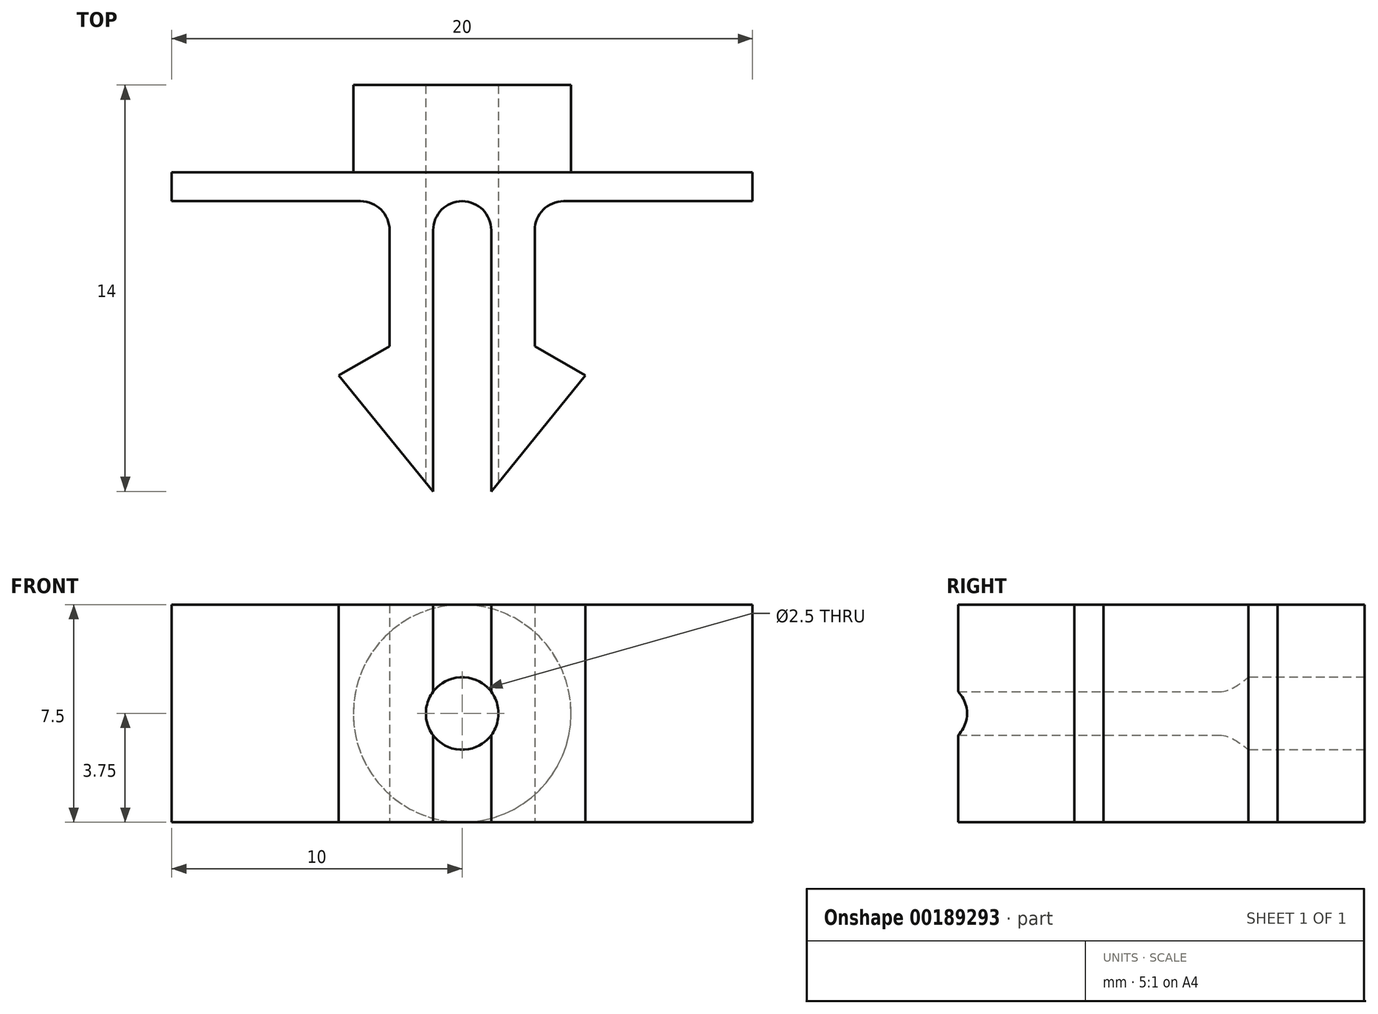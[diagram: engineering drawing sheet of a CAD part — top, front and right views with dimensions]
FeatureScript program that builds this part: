
annotation { "Feature Type Name" : "Feature", "Feature Type Description" : "" }
export const myFeature = defineFeature(function(context is Context, id is Id, definition is map)
    precondition{}
    {
        {
            var Q0;
            Q0=qCreatedBy(makeId("Top.planeOp"),FACE);
            var sketch = newSketch(context, id + "F0", { "sketchPlane" : qUnion([Q0])});
            skLineSegment(sketch, "E0", {"start": v(-1, 0) * mm, "end": v(-1, 9) * mm});
            skLineSegment(sketch, "E1", {"start": v(1, 9) * mm, "end": v(1, 0) * mm});
            skPoint(sketch, "E2", {"position": v(-1, 5) * mm});
            skPoint(sketch, "E3", {"position": v(1, 5) * mm});
            skLineSegment(sketch, "E4", {"start": v(-2.5, 5) * mm, "end": v(-2.5, 10) * mm});
            skLineSegment(sketch, "E5", {"start": v(2.5, 10) * mm, "end": v(2.5, 5) * mm});
            skLineSegment(sketch, "E6", {"start": v(-4.25, 4) * mm, "end": v(4.25, 4) * mm, "construction": true});
            skPoint(sketch, "E7", {"position": v(0, 4) * mm});
            skArc(sketch, "E8", {"start": v(1, 9) * mm, "mid": v(0, 10) * mm, "end": v(-1, 9) * mm});
            skLineSegment(sketch, "E9", {"start": v(1, 0) * mm, "end": v(4.25, 4) * mm});
            skLineSegment(sketch, "E10", {"start": v(2.5, 5) * mm, "end": v(4.25, 4) * mm});
            skLineSegment(sketch, "E11", {"start": v(-2.5, 5) * mm, "end": v(-4.25, 4) * mm});
            skLineSegment(sketch, "E12", {"start": v(-4.25, 4) * mm, "end": v(-1, 0) * mm});
            skLineSegment(sketch, "E13", {"start": v(-2.5, 10) * mm, "end": v(-10, 10) * mm});
            skLineSegment(sketch, "E14", {"start": v(-10, 10) * mm, "end": v(-10, 11) * mm});
            skLineSegment(sketch, "E15", {"start": v(-10, 11) * mm, "end": v(10, 11) * mm});
            skLineSegment(sketch, "E16", {"start": v(10, 11) * mm, "end": v(10, 10) * mm});
            skLineSegment(sketch, "E17", {"start": v(10, 10) * mm, "end": v(2.5, 10) * mm});
            skPoint(sketch, "E18", {"position": v(0, 11) * mm});
            skPoint(sketch, "E19", {"position": v(0, 10) * mm});
            skSolve(sketch);
        }
        {
            var Q0;
            Q0=makeQuery(id+"F0.imprint","IMPRINT",FACE,{"disambiguationData":[TD([[makeQuery(id+"F0.imprint","IMPRINT",EDGE,{"derivedFrom":sQuery(id+"F0.wireOp",EDGE,"E0")}),1.0]])]});
            extrude(context, id + "F1", {"entities" : qUnion([Q0]), "depth" : 7.5 * mm});
        }
        {
            var Q0;
            Q0=makeQuery(id+"F1.opExtrude","SWEPT_EDGE",EDGE,{"disambiguationData":[OSD([sQuery(id+"F0.wireOp",EDGE,"E5"),sQuery(id+"F0.wireOp",EDGE,"E17")])]});
            var Q1;
            Q1=makeQuery(id+"F1.opExtrude","SWEPT_EDGE",EDGE,{"disambiguationData":[OSD([sQuery(id+"F0.wireOp",EDGE,"E4"),sQuery(id+"F0.wireOp",EDGE,"E13")])]});
            fillet(context, id + "F2", {"entities" : qUnion([Q0, Q1]), "radius" : 1 * mm, "tangentPropagation" : true, "allowEdgeOverflow" : false});
        }
        {
            var Q0;
            Q0=makeQuery(id+"F1.opExtrude","SWEPT_FACE",FACE,{"disambiguationData":[OSD([sQuery(id+"F0.wireOp",EDGE,"E15")])]});
            var sketch = newSketch(context, id + "F3", { "sketchPlane" : qUnion([Q0])});
            skLineSegment(sketch, "E20", {"start": v(0, 7.5) * mm, "end": v(0, 0) * mm, "construction": true});
            skPoint(sketch, "E21", {"position": v(0, 3.75) * mm});
            skCircle(sketch, "E22", {"center": v(0, 3.75) * mm, "radius": 3.75 * mm});
            skCircle(sketch, "E23", {"center": v(0, 3.75) * mm, "radius": 1.25 * mm});
            skSolve(sketch);
        }
        {
            var Q0;
            {var subQ0=sQuery(id+"F3.wireOp",EDGE,"E22");var subQ1=sQuery(id+"F0.wireOp",EDGE,"E15");var subQ2=makeQuery(id+"F3.imprint","INTERSECT",VERTEX,{"derivedFrom":[makeQuery(id+"F1.opExtrude","CAP_EDGE",EDGE,{"disambiguationData":[OSD([subQ1])],"isStart":true}),subQ0]});Q0=makeQuery(id+"F3.imprint","IMPRINT",FACE,{"disambiguationData":[TD([[makeQuery(id+"F3.imprint","IMPRINT",EDGE,{"disambiguationData":[TD([[subQ2,1.0]])],"derivedFrom":subQ0}),1.0]])]});}
            extrude(context, id + "F4", {"entities" : qUnion([Q0]), "operationType" : NewBodyOperationType.ADD, "depth" : 3 * mm});
        }
        {
            var Q0;
            Q0=makeQuery(id+"F3.imprint","IMPRINT",FACE,{"disambiguationData":[TD([[makeQuery(id+"F3.imprint","IMPRINT",EDGE,{"derivedFrom":sQuery(id+"F3.wireOp",EDGE,"E23")}),1.0]])]});
            var Q1;
            Q1=makeQuery(id+"F1.opExtrude","SWEPT_FACE",FACE,{"disambiguationData":[OSD([sQuery(id+"F0.wireOp",EDGE,"E8")])]});
            extrude(context, id + "F5", {"entities" : qUnion([Q0]), "operationType" : NewBodyOperationType.REMOVE, "oppositeDirection" : true, "endBoundEntityFace" : qUnion([Q1]), "depth" : 13 * mm});
        }
    });
